# Revit family: Faucet-Lavatory-KOHLER-Triton_Bowe-K-100T70
name_source: partatom
category: Plumbing Fixtures
units: mm (PartAtom-declared; Revit-internal decimal feet)

## family parameters
Cut with Voids When Loaded = No
Host = Face
OmniClass Number = 23.31.11.00
Part Type = Normal
Room Calculation Point = No
Round Connector Dimension = Use Diameter
Shared = No

## types (1)
- Not a Type-See Type Catalog
    ADA Compliant = Yes
    Assembly Code = D2010
    CW Connection = Yes
    Cold Water Inlet = Cold Water Inlet
    Date Modified = 6/14/2019
    Default Elevation = 36"
    Description = 0.5 gpm monoblock gooseneck bathroom sink faucet with laminar flow and wristblade handles, drain not included
    Drain Included = No
    Edition number = 1
    Finish = Default
    Flow Rate = 1 GPM
    HW Connection = Yes
    Handle Clearance = 4 1/16"
    Height = 16 5/8"
    Hot Water Inlet = Hot Water Inlet
    Length = 5 1/4"
    Lever Handles = No
    Manufacturer = KOHLER Co.
    MasterFormat 1995 = 15410
    MasterFormat 2004 = 22.41.39
    Material = Brass Construction
    Model = K-100T70-5ANL-CP
    Overall Width = 9 3/4"
    Pressure = 60.00 psi
    Product Documentation Link = https://www.us.kohler.com
    Product Guid = 8a29a1ee-2f28-4f77-a818-3810a4f95964
    Product Name = Triton Bowe
    Product Page URL = http://www.us.kohler.com
    Product data url = https://bimobject.com
    Spout Reach = 5 1/4"
    Type = 1
    URL = https://www.us.kohler.com
    Vent Connection = No
    Waste Connection = No
    Waste Water Outlet = Waste Water Outlet
    WaterSense Certified = No
    Width = 2 1/4"
    Wristblade Handles = Yes

## geometry (parser evidence)
native form markers: Sweep x4
no freeform markers — native parametric forms only
